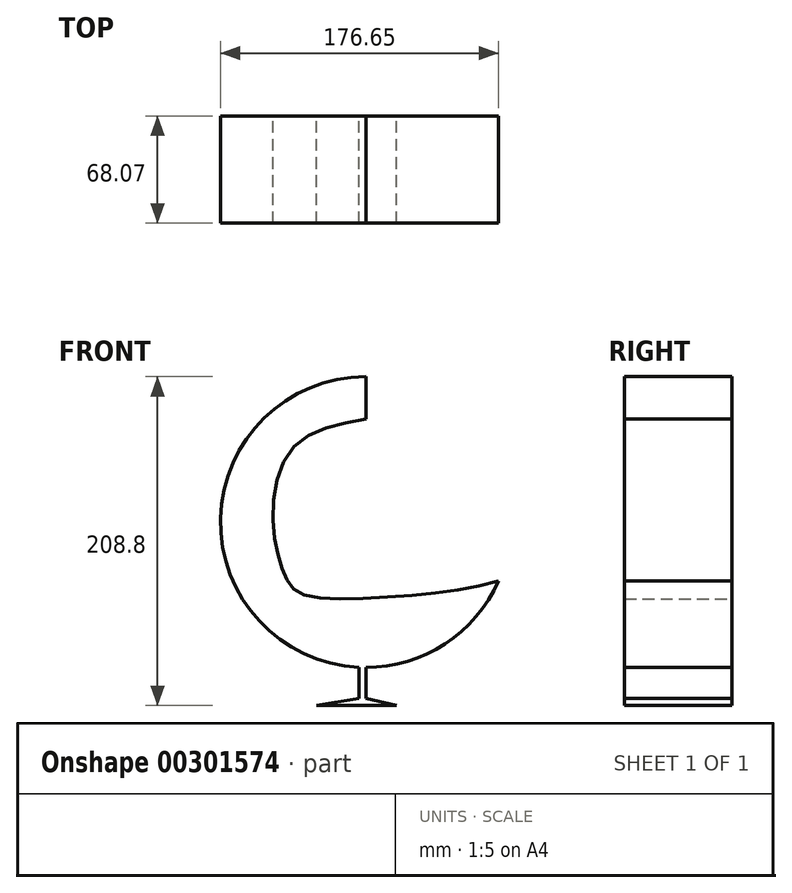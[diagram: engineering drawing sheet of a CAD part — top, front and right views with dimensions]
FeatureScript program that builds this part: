
annotation { "Feature Type Name" : "Feature", "Feature Type Description" : "" }
export const myFeature = defineFeature(function(context is Context, id is Id, definition is map)
    precondition{}
    {
        {
            var Q0;
            Q0=qCreatedBy(makeId("Front.planeOp"),FACE);
            var sketch = newSketch(context, id + "F0", { "sketchPlane" : qUnion([Q0])});
            skArc(sketch, "E0", {"start": v(0, 92.3) * mm, "mid": v(-77.38, -50.3) * mm, "end": v(84.35, -37.46) * mm});
            skFitSpline(sketch, "E1", {"points": [v(84.35, -37.46) * mm, v(17.96, -47.41) * mm, v(-40.4, -45.73) * mm, v(-51.62, -33.39) * mm, v(-58.92, 0) * mm, v(-46.01, 47.41) * mm, v(0, 65.37) * mm], "startDerivative": vector(-273.11, -86.02) * mm, "endDerivative": vector(297.97, 54.57) * mm});
            skLineSegment(sketch, "E2", {"start": v(0, 65.37) * mm, "end": v(0, 92.3) * mm});
            skLineSegment(sketch, "E3", {"start": v(-4.39, -92.2) * mm, "end": v(-4.39, -112.1) * mm});
            skLineSegment(sketch, "E4", {"start": v(-4.39, -112.1) * mm, "end": v(-31.38, -116.5) * mm});
            skLineSegment(sketch, "E5", {"start": v(-31.38, -116.5) * mm, "end": v(19.42, -116.5) * mm});
            skLineSegment(sketch, "E6", {"start": v(19.42, -116.5) * mm, "end": v(0, -112.1) * mm});
            skLineSegment(sketch, "E7", {"start": v(0, -112.1) * mm, "end": v(0, -92.3) * mm});
            skLineSegment(sketch, "E8", {"start": v(0, -92.3) * mm, "end": v(0, -121.56) * mm, "construction": true});
            skSolve(sketch);
        }
        {
            var Q0;
            Q0=makeQuery(id+"F0.imprint","IMPRINT",FACE,{"disambiguationData":[TD([[makeQuery(id+"F0.imprint","IMPRINT",EDGE,{"derivedFrom":sQuery(id+"F0.wireOp",EDGE,"E0")}),1.0]])]});
            extrude(context, id + "F1", {"entities" : qUnion([Q0]), "depth" : 51.05 * mm});
        }
        {
            var Q0;
            Q0 = qSketchRegion(id + "F0", true);
            extrude(context, id + "F2", {"entities" : qUnion([Q0]), "operationType" : NewBodyOperationType.ADD, "depth" : 68.07 * mm});
        }
    });
